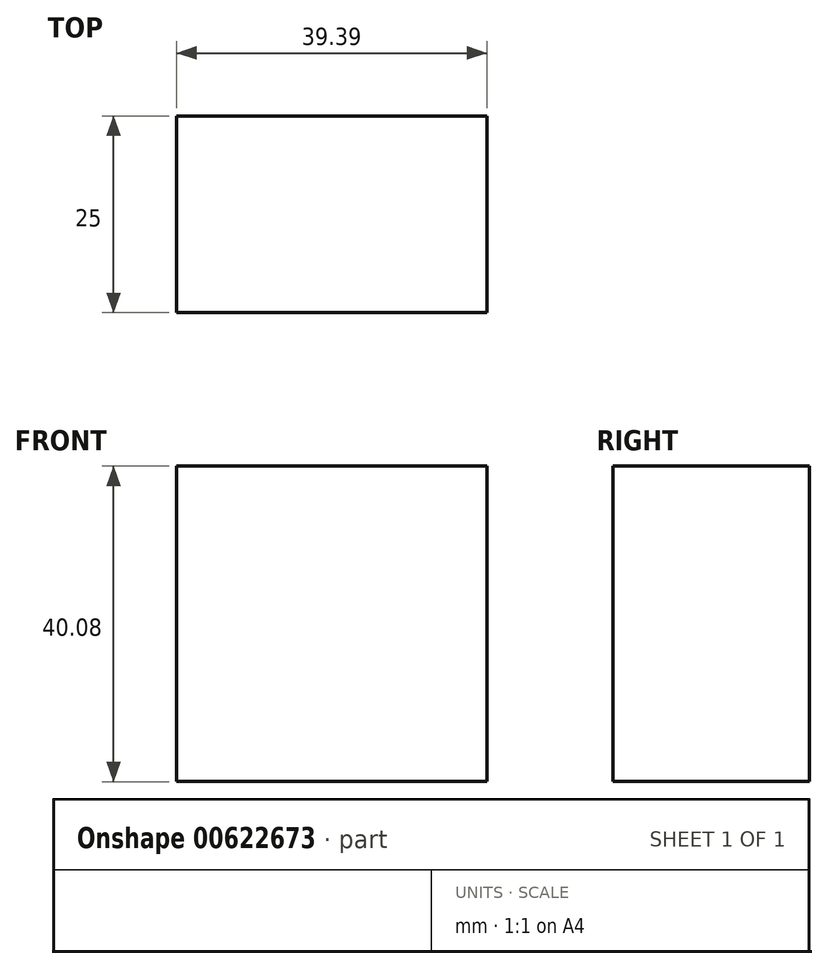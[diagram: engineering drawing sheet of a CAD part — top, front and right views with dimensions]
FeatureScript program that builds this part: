
annotation { "Feature Type Name" : "Feature", "Feature Type Description" : "" }
export const myFeature = defineFeature(function(context is Context, id is Id, definition is map)
    precondition{}
    {
        {
            var Q0;
            Q0=qCreatedBy(makeId("Front.planeOp"),FACE);
            var sketch = newSketch(context, id + "F0", { "sketchPlane" : qUnion([Q0])});
            skLineSegment(sketch, "E0.bottom", {"start": v(-103.14, 5.77) * mm, "end": v(-63.75, 5.77) * mm});
            skLineSegment(sketch, "E0.top", {"start": v(-103.14, 45.85) * mm, "end": v(-63.75, 45.85) * mm});
            skLineSegment(sketch, "E0.left", {"start": v(-103.14, 5.77) * mm, "end": v(-103.14, 45.85) * mm});
            skLineSegment(sketch, "E0.right", {"start": v(-63.75, 5.77) * mm, "end": v(-63.75, 45.85) * mm});
            skPoint(sketch, "E0.middle", {"position": v(-83.45, 25.81) * mm});
            skSolve(sketch);
        }
        {
            var Q0;
            Q0=makeQuery(id+"F0.imprint","IMPRINT",FACE,{"disambiguationData":[TD([[makeQuery(id+"F0.imprint","IMPRINT",EDGE,{"derivedFrom":sQuery(id+"F0.wireOp",EDGE,"E0.bottom")}),1.0]])]});
            extrude(context, id + "F1", {"entities" : qUnion([Q0]), "depth" : 25 * mm, "offsetDistance" : 25 * mm});
        }
    });
